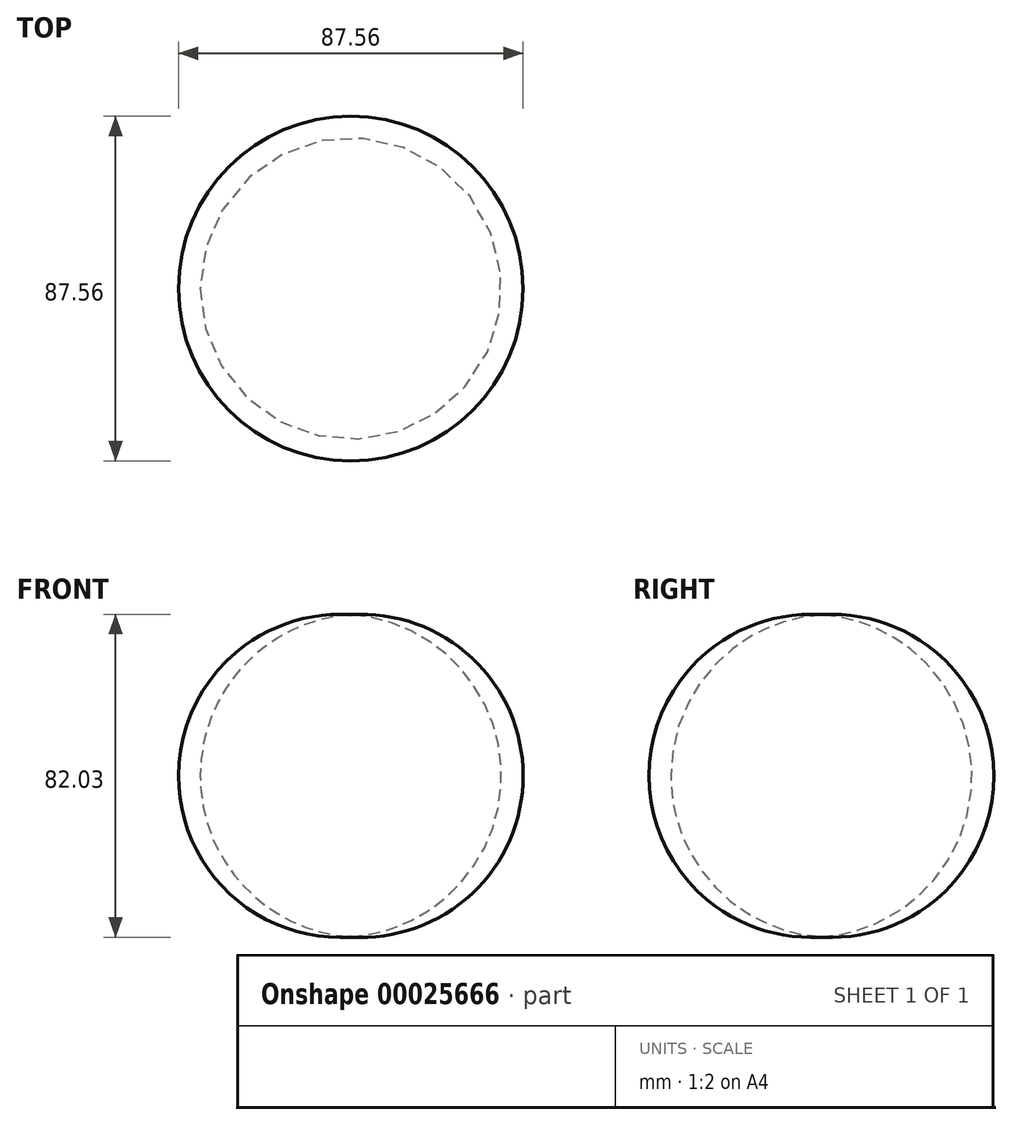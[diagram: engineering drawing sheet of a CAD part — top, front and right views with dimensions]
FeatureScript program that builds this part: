
annotation { "Feature Type Name" : "Feature", "Feature Type Description" : "" }
export const myFeature = defineFeature(function(context is Context, id is Id, definition is map)
    precondition{}
    {
        {
            var Q0;
            Q0=qCreatedBy(makeId("Front.planeOp"),FACE);
            var sketch = newSketch(context, id + "F0", { "sketchPlane" : qUnion([Q0])});
            skArc(sketch, "E0", {"start": v(0, 45.04) * mm, "mid": v(-43.78, 4.11) * mm, "end": v(0, -36.81) * mm});
            skLineSegment(sketch, "E1", {"start": v(0, 0) * mm, "end": v(0, 102.64) * mm});
            skSolve(sketch);
        }
        {
            var Q0;
            Q0=sQuery(id+"F0.wireOp",EDGE,"E0");
            var Q1;
            Q1=sQuery(id+"F0.wireOp",EDGE,"E1");
            revolve(context, id + "F1", {"bodyType" : ToolBodyType.SURFACE, "surfaceEntities" : qUnion([Q0]), "axis" : qUnion([Q1]), "revolveType" : RevolveType.FULL});
        }
    });
